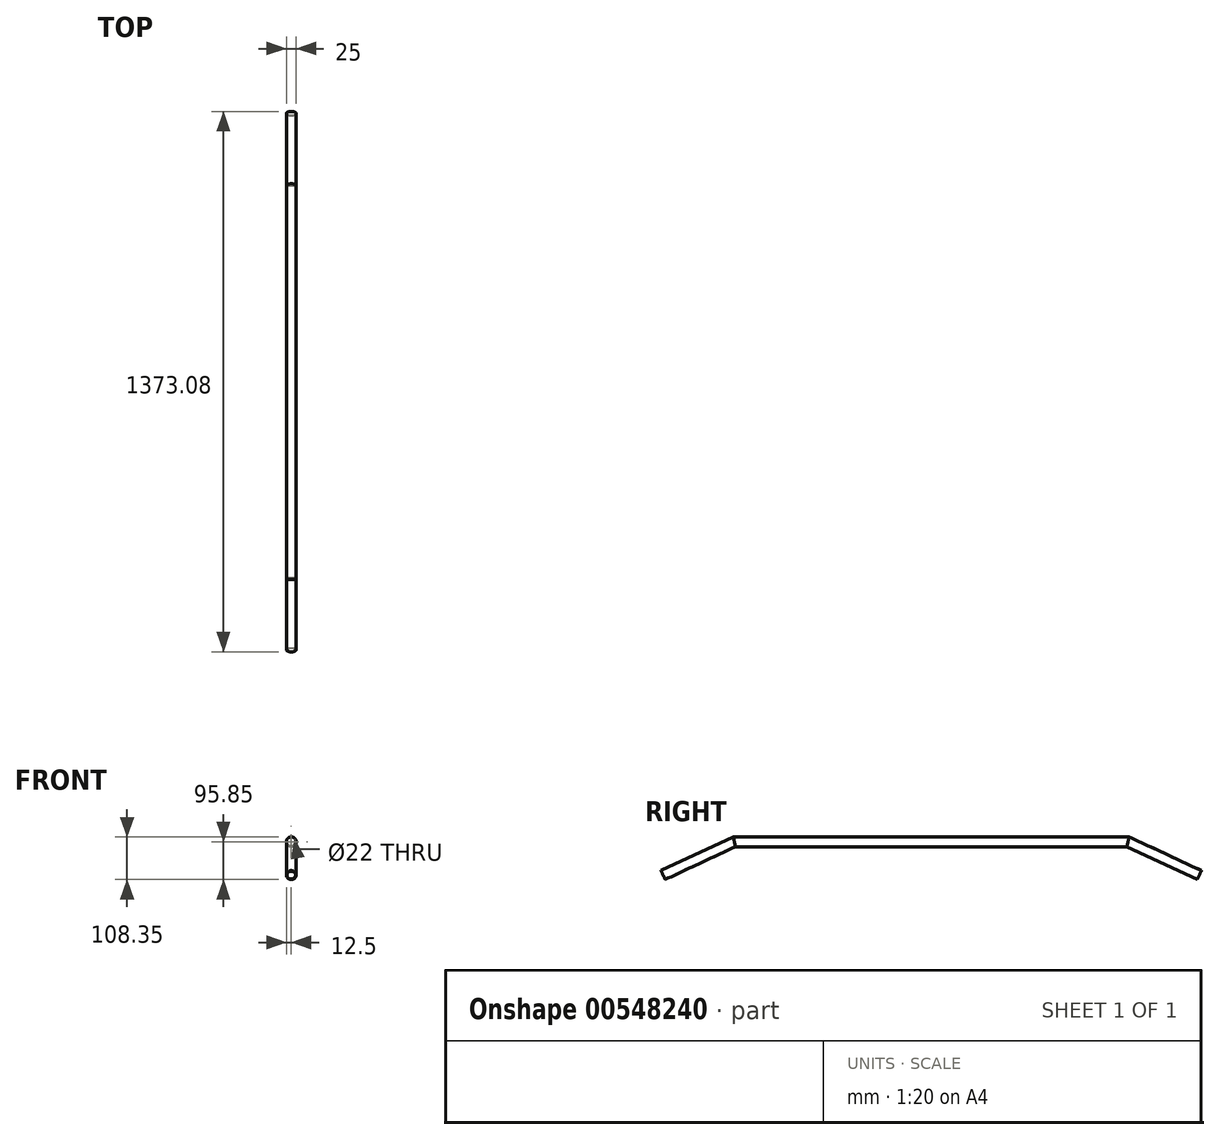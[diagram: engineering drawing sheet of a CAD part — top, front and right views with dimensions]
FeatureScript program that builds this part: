
annotation { "Feature Type Name" : "Feature", "Feature Type Description" : "" }
export const myFeature = defineFeature(function(context is Context, id is Id, definition is map)
    precondition{}
    {
        {
            var Q0;
            Q0=qCreatedBy(makeId("Front.planeOp"),FACE);
            var sketch = newSketch(context, id + "F0", { "sketchPlane" : qUnion([Q0])});
            skCircle(sketch, "E0", {"center": v(0, 0) * mm, "radius": 12.5 * mm});
            skCircle(sketch, "E1.0", {"center": v(0, 0) * mm, "radius": 11 * mm});
            skSolve(sketch);
        }
        {
            var Q0;
            Q0=qCreatedBy(makeId("Right.planeOp"),FACE);
            var sketch = newSketch(context, id + "F1", { "sketchPlane" : qUnion([Q0])});
            skLineSegment(sketch, "E2", {"start": v(0, 0) * mm, "end": v(-500, 0) * mm});
            skLineSegment(sketch, "E3", {"start": v(-500, 0) * mm, "end": v(-681.26, -84.52) * mm});
            skLineSegment(sketch, "E4.MirrorCS", {"start": v(500, 0) * mm, "end": v(681.26, -84.52) * mm});
            skLineSegment(sketch, "E5.MirrorCS", {"start": v(0, 0) * mm, "end": v(500, 0) * mm});
            skSolve(sketch);
        }
        {
            var Q0;
            Q0=makeQuery(id+"F0.imprint","IMPRINT",FACE,{"disambiguationData":[TD([[makeQuery(id+"F0.imprint","IMPRINT",EDGE,{"derivedFrom":sQuery(id+"F0.wireOp",EDGE,"E0")}),1.0]])]});
            var Q1;
            Q1=sQuery(id+"F1.wireOp",EDGE,"E5.MirrorCS");
            var Q2;
            Q2=sQuery(id+"F1.wireOp",EDGE,"E4.MirrorCS");
            sweep(context, id + "F2", {"profiles" : qUnion([Q0]), "path" : qUnion([Q1, Q2])});
        }
        {
            var Q0;
            Q0=makeQuery(id+"F0.imprint","IMPRINT",FACE,{"disambiguationData":[TD([[makeQuery(id+"F0.imprint","IMPRINT",EDGE,{"derivedFrom":sQuery(id+"F0.wireOp",EDGE,"E0")}),1.0]])]});
            var Q1;
            Q1=sQuery(id+"F1.wireOp",EDGE,"E2");
            var Q2;
            Q2=sQuery(id+"F1.wireOp",EDGE,"E3");
            sweep(context, id + "F3", {"operationType" : NewBodyOperationType.ADD, "profiles" : qUnion([Q0]), "path" : qUnion([Q1, Q2])});
        }
    });
